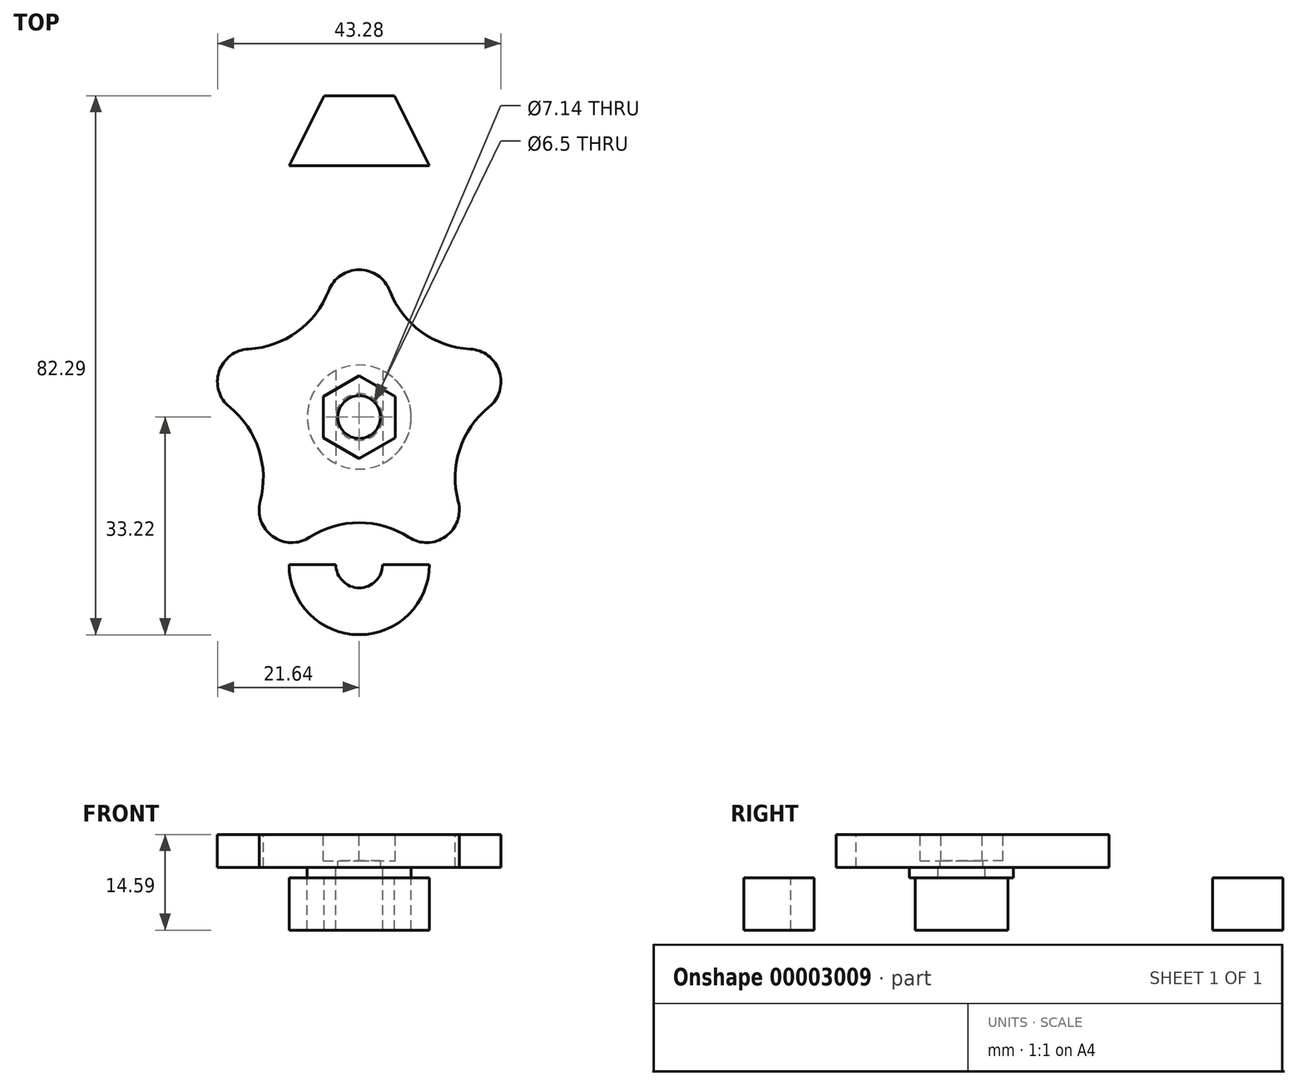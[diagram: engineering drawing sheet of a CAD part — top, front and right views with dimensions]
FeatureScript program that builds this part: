
annotation { "Feature Type Name" : "Feature", "Feature Type Description" : "" }
export const myFeature = defineFeature(function(context is Context, id is Id, definition is map)
    precondition{}
    {
        {
            var Q0;
            Q0=qCreatedBy(makeId("Top.planeOp"),FACE);
            var sketch = newSketch(context, id + "F0", { "sketchPlane" : qUnion([Q0])});
            skCircle(sketch, "E0.cCircle", {"center": v(0, 0) * mm, "radius": 14.16 * mm, "construction": true});
            skLineSegment(sketch, "E0.0", {"start": v(0, 17.5) * mm, "end": v(16.64, 5.4) * mm, "construction": true});
            skLineSegment(sketch, "E0.1", {"start": v(16.64, 5.4) * mm, "end": v(10.29, -14.16) * mm, "construction": true});
            skLineSegment(sketch, "E0.2", {"start": v(10.29, -14.16) * mm, "end": v(-10.29, -14.16) * mm, "construction": true});
            skLineSegment(sketch, "E0.3", {"start": v(-10.29, -14.16) * mm, "end": v(-16.64, 5.4) * mm, "construction": true});
            skLineSegment(sketch, "E0.4", {"start": v(-16.64, 5.4) * mm, "end": v(0, 17.5) * mm, "construction": true});
            skPoint(sketch, "E0.0.midPoint", {"position": v(8.32, 11.45) * mm});
            skCircle(sketch, "E1", {"center": v(0, 17.5) * mm, "radius": 5 * mm});
            skCircle(sketch, "E2", {"center": v(16.64, 5.4) * mm, "radius": 5 * mm});
            skCircle(sketch, "E3", {"center": v(10.29, -14.16) * mm, "radius": 5 * mm});
            skCircle(sketch, "E4", {"center": v(-10.29, -14.16) * mm, "radius": 5 * mm});
            skCircle(sketch, "E5", {"center": v(-16.64, 5.4) * mm, "radius": 5 * mm});
            skLineSegment(sketch, "E6", {"start": v(-10.29, -19.16) * mm, "end": v(10.29, -19.16) * mm, "construction": true});
            skArc(sketch, "E7", {"start": v(-16.9, 10.4) * mm, "mid": v(-9.47, 13.03) * mm, "end": v(-4.67, 19.3) * mm});
            skArc(sketch, "E8", {"start": v(4.67, 19.3) * mm, "mid": v(9.47, 13.03) * mm, "end": v(16.9, 10.4) * mm});
            skArc(sketch, "E9", {"start": v(19.8, 1.52) * mm, "mid": v(15.32, -4.98) * mm, "end": v(15.12, -12.86) * mm});
            skArc(sketch, "E10", {"start": v(7.56, -18.35) * mm, "mid": v(0, -16.11) * mm, "end": v(-7.56, -18.35) * mm});
            skArc(sketch, "E11", {"start": v(-15.12, -12.86) * mm, "mid": v(-15.32, -4.98) * mm, "end": v(-19.8, 1.52) * mm});
            skCircle(sketch, "E12", {"center": v(0, 0) * mm, "radius": 30 * mm, "construction": true});
            skCircle(sketch, "E13", {"center": v(0, 0) * mm, "radius": 22.5 * mm, "construction": true});
            skCircle(sketch, "E14.cCircle", {"center": v(0, 0) * mm, "radius": 5.48 * mm, "construction": true});
            skLineSegment(sketch, "E14.0", {"start": v(0, 6.33) * mm, "end": v(5.48, 3.16) * mm});
            skLineSegment(sketch, "E14.1", {"start": v(5.48, 3.16) * mm, "end": v(5.48, -3.16) * mm});
            skLineSegment(sketch, "E14.2", {"start": v(5.48, -3.16) * mm, "end": v(0, -6.33) * mm});
            skLineSegment(sketch, "E14.3", {"start": v(0, -6.33) * mm, "end": v(-5.48, -3.16) * mm});
            skLineSegment(sketch, "E14.4", {"start": v(-5.48, -3.16) * mm, "end": v(-5.48, 3.16) * mm});
            skLineSegment(sketch, "E14.5", {"start": v(-5.48, 3.16) * mm, "end": v(0, 6.33) * mm});
            skPoint(sketch, "E14.0.midPoint", {"position": v(2.74, 4.75) * mm});
            skCircle(sketch, "E15", {"center": v(0, 0) * mm, "radius": 3.25 * mm});
            skSolve(sketch);
        }
        {
            var Q0;
            Q0 = qSketchRegion(id + "F0", true);
            var Q1;
            Q1=makeQuery(id+"F0.imprint","IMPRINT",FACE,{"disambiguationData":[TD([[makeQuery(id+"F0.imprint","IMPRINT",EDGE,{"derivedFrom":sQuery(id+"F0.wireOp",EDGE,"E14.0")}),-1.0]])]});
            extrude(context, id + "F1", {"entities" : qUnion([Q0, Q1]), "oppositeDirection" : true, "depth" : 5 * mm});
        }
        {
            var Q0;
            Q0=makeQuery(id+"F0.imprint","IMPRINT",FACE,{"disambiguationData":[TD([[makeQuery(id+"F0.imprint","IMPRINT",EDGE,{"derivedFrom":sQuery(id+"F0.wireOp",EDGE,"E14.0")}),-1.0]])]});
            extrude(context, id + "F2", {"entities" : qUnion([Q0]), "operationType" : NewBodyOperationType.REMOVE, "oppositeDirection" : true, "depth" : 4 * mm});
        }
        {
            var Q0;
            Q0=makeQuery(id+"F1.opExtrude","CAP_FACE",FACE,{"disambiguationData":[OSD([sQuery(id+"F0.wireOp",EDGE,"E1"),sQuery(id+"F0.wireOp",EDGE,"E2"),sQuery(id+"F0.wireOp",EDGE,"E3"),sQuery(id+"F0.wireOp",EDGE,"E4"),sQuery(id+"F0.wireOp",EDGE,"E5"),sQuery(id+"F0.wireOp",EDGE,"E7"),sQuery(id+"F0.wireOp",EDGE,"E8"),sQuery(id+"F0.wireOp",EDGE,"E9"),sQuery(id+"F0.wireOp",EDGE,"E10"),sQuery(id+"F0.wireOp",EDGE,"E11"),sQuery(id+"F0.wireOp",EDGE,"E15")])],"isStart":false});
            var sketch = newSketch(context, id + "F3", { "sketchPlane" : qUnion([Q0])});
            skCircle(sketch, "E16", {"center": v(0, 0) * mm, "radius": 7.94 * mm});
            skCircle(sketch, "E17", {"center": v(0, 0) * mm, "radius": 3.57 * mm});
            skSolve(sketch);
        }
        {
            var Q0;
            Q0=makeQuery(id+"F3.imprint","IMPRINT",FACE,{"disambiguationData":[TD([[makeQuery(id+"F3.imprint","IMPRINT",EDGE,{"derivedFrom":sQuery(id+"F3.wireOp",EDGE,"E16")}),1.0]])]});
            extrude(context, id + "F4", {"entities" : qUnion([Q0]), "depth" : (1 / 16 * 25.4) * mm});
        }
        {
            var Q0;
            Q0=makeQuery(id+"F4.opExtrude","CAP_FACE",FACE,{"disambiguationData":[OSD([sQuery(id+"F3.wireOp",EDGE,"E16"),sQuery(id+"F3.wireOp",EDGE,"E17")])],"isStart":false});
            var sketch = newSketch(context, id + "F5", { "sketchPlane" : qUnion([Q0])});
            skLineSegment(sketch, "E18.rect.bottom", {"start": v(3.57, -22.5) * mm, "end": v(-3.57, -22.5) * mm});
            skLineSegment(sketch, "E18.rect.top", {"start": v(3.57, 22.5) * mm, "end": v(-3.57, 22.5) * mm});
            skLineSegment(sketch, "E18.rect.left", {"start": v(3.57, -22.5) * mm, "end": v(3.57, 22.5) * mm});
            skLineSegment(sketch, "E18.rect.right", {"start": v(-3.57, -22.5) * mm, "end": v(-3.57, 22.5) * mm});
            skPoint(sketch, "E18.rect.middle", {"position": v(0, 0) * mm});
            skLineSegment(sketch, "E19.bottom", {"start": v(-10.72, -38.36) * mm, "end": v(10.72, -38.36) * mm});
            skLineSegment(sketch, "E19.top", {"start": v(-10.72, 22.5) * mm, "end": v(10.72, 22.5) * mm});
            skLineSegment(sketch, "E19.left", {"start": v(-10.72, -38.36) * mm, "end": v(-10.72, 22.5) * mm});
            skLineSegment(sketch, "E19.right", {"start": v(10.72, -38.36) * mm, "end": v(10.72, 22.5) * mm});
            skArc(sketch, "E20", {"start": v(-3.57, -22.5) * mm, "mid": v(0, -26.07) * mm, "end": v(3.57, -22.5) * mm});
            skArc(sketch, "E21", {"start": v(3.57, 22.5) * mm, "mid": v(0, 26.07) * mm, "end": v(-3.57, 22.5) * mm});
            skLineSegment(sketch, "E22", {"start": v(-10.72, -38.36) * mm, "end": v(-5.36, -49.07) * mm});
            skLineSegment(sketch, "E23", {"start": v(-5.36, -49.07) * mm, "end": v(5.36, -49.07) * mm});
            skLineSegment(sketch, "E24", {"start": v(5.36, -49.07) * mm, "end": v(10.72, -38.36) * mm});
            skPoint(sketch, "E25", {"position": v(0, -49.07) * mm});
            skLineSegment(sketch, "E26", {"start": v(-10.72, -38.36) * mm, "end": v(0, -38.36) * mm, "construction": true});
            skLineSegment(sketch, "E27", {"start": v(0, -38.36) * mm, "end": v(0, -49.07) * mm, "construction": true});
            skArc(sketch, "E28", {"start": v(10.72, 22.5) * mm, "mid": v(0, 33.22) * mm, "end": v(-10.72, 22.5) * mm});
            skLineSegment(sketch, "E29", {"start": v(3.57, 0) * mm, "end": v(10.72, 0) * mm, "construction": true});
            skLineSegment(sketch, "E30", {"start": v(-3.57, 0) * mm, "end": v(-10.72, 0) * mm, "construction": true});
            skLineSegment(sketch, "E31", {"start": v(3.57, 0) * mm, "end": v(-3.57, 0) * mm, "construction": true});
            skSolve(sketch);
        }
        {
            var Q0;
            Q0=makeQuery(id+"F5.imprint","IMPRINT",FACE,{"disambiguationData":[TD([[makeQuery(id+"F5.imprint","IMPRINT",EDGE,{"derivedFrom":sQuery(id+"F5.wireOp",EDGE,"E19.bottom")}),-1.0]])]});
            var Q1;
            Q1=makeQuery(id+"F5.imprint","IMPRINT",FACE,{"disambiguationData":[TD([[makeQuery(id+"F5.imprint","IMPRINT",EDGE,{"derivedFrom":sQuery(id+"F5.wireOp",EDGE,"E19.top")}),1.0]])]});
            var Q2;
            {var subQ0=makeQuery(id+"F4.opExtrude","CAP_EDGE",EDGE,{"disambiguationData":[OSD([sQuery(id+"F3.wireOp",EDGE,"E16")])],"isStart":false});var subQ1=sQuery(id+"F5.wireOp",EDGE,"E18.rect.left");var subQ4=makeQuery(id+"F5.imprint","INTERSECT",VERTEX,{"disambiguationData":[OD(0.0)],"derivedFrom":[subQ0,subQ1]});Q2=makeQuery(id+"F5.imprint","IMPRINT",FACE,{"disambiguationData":[TD([[makeQuery(id+"F5.imprint","IMPRINT",EDGE,{"disambiguationData":[TD([[subQ4,-1.0]])],"derivedFrom":subQ1}),-1.0]])]});}
            var Q3;
            {var subQ0=makeQuery(id+"F4.opExtrude","CAP_EDGE",EDGE,{"disambiguationData":[OSD([sQuery(id+"F3.wireOp",EDGE,"E16")])],"isStart":false});var subQ1=sQuery(id+"F5.wireOp",EDGE,"E18.rect.right");var subQ4=makeQuery(id+"F5.imprint","INTERSECT",VERTEX,{"disambiguationData":[OD(0.0)],"derivedFrom":[subQ0,subQ1]});Q3=makeQuery(id+"F5.imprint","IMPRINT",FACE,{"disambiguationData":[TD([[makeQuery(id+"F5.imprint","IMPRINT",EDGE,{"disambiguationData":[TD([[subQ4,-1.0]])],"derivedFrom":subQ1}),1.0]])]});}
            var Q4;
            {var subQ10=sQuery(id+"F5.wireOp",EDGE,"E19.bottom");Q4=makeQuery(id+"F5.imprint","IMPRINT",FACE,{"disambiguationData":[TD([[makeQuery(id+"F5.imprint","IMPRINT",EDGE,{"derivedFrom":subQ10}),1.0]])]});}
            extrude(context, id + "F6", {"entities" : qUnion([Q0, Q1, Q2, Q3, Q4]), "depth" : 8 * mm});
        }
    });
